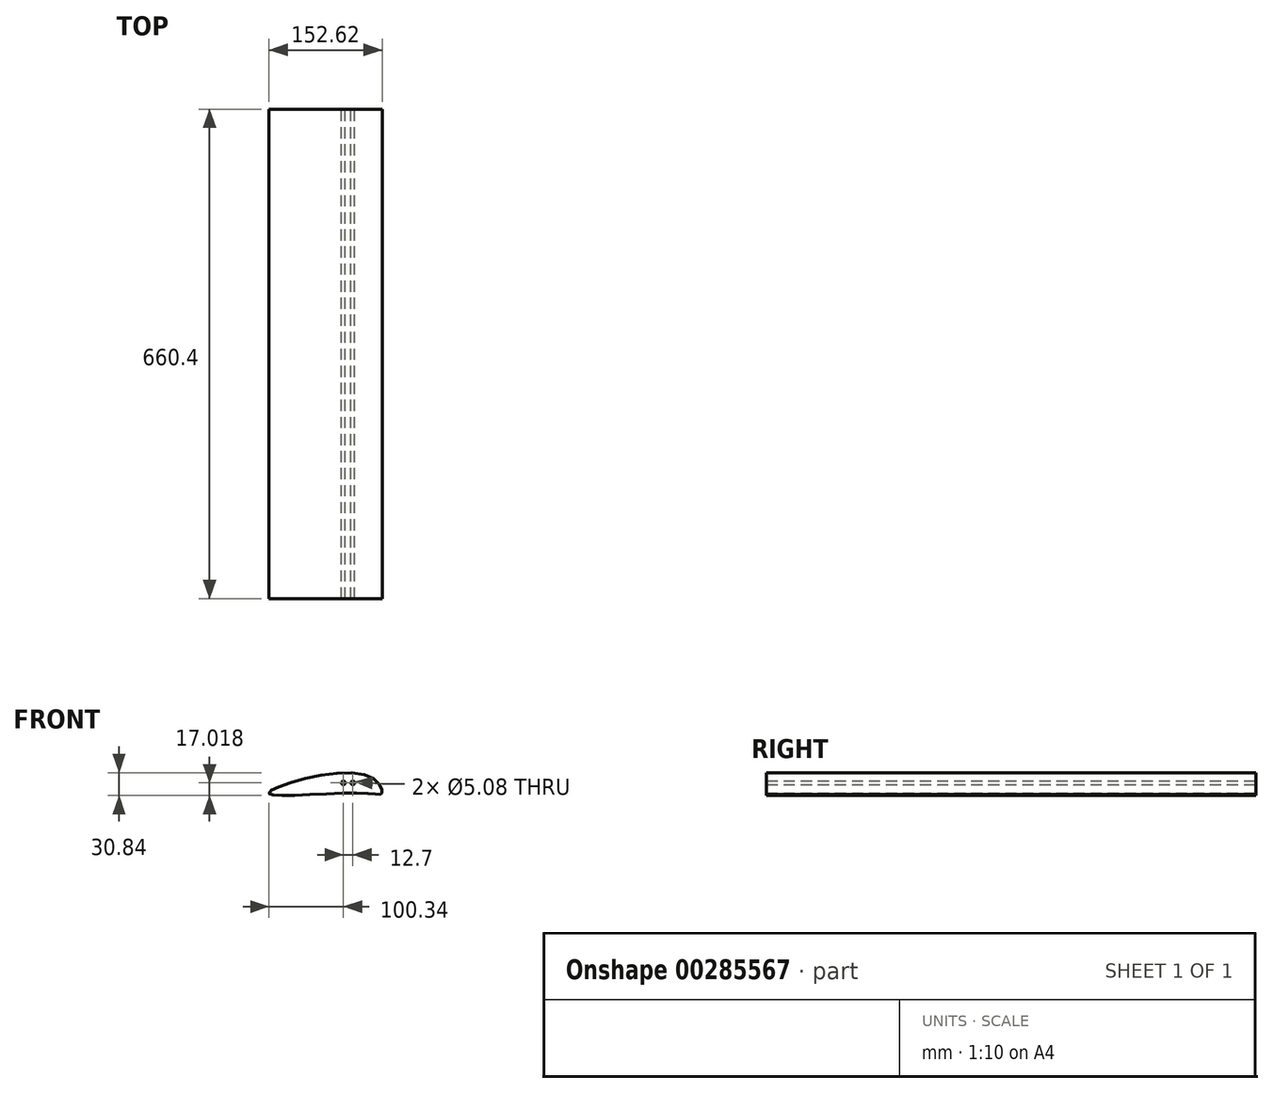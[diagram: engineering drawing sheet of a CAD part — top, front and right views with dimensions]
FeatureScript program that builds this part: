
annotation { "Feature Type Name" : "Feature", "Feature Type Description" : "" }
export const myFeature = defineFeature(function(context is Context, id is Id, definition is map)
    precondition{}
    {
        {
            var Q0;
            Q0=qCreatedBy(makeId("Front.planeOp"),FACE);
            var sketch = newSketch(context, id + "F0", { "sketchPlane" : qUnion([Q0])});
            skFitSpline(sketch, "E0", {"points": [v(39.37, 0) * mm, v(14.25, 25.4) * mm, v(-113.03, 0) * mm, v(15.39, 0) * mm, v(39.37, 0) * mm]});
            skLineSegment(sketch, "E1", {"start": v(0, 0) * mm, "end": v(0, 47.84) * mm, "construction": true});
            skLineSegment(sketch, "E2", {"start": v(-12.7, 43.07) * mm, "end": v(-12.7, -19.6) * mm, "construction": true});
            skLineSegment(sketch, "E3", {"start": v(-20.65, 13.74) * mm, "end": v(12.68, 13.74) * mm, "construction": true});
            skCircle(sketch, "E4", {"center": v(0, 13.74) * mm, "radius": 2.54 * mm});
            skCircle(sketch, "E5", {"center": v(-12.7, 13.74) * mm, "radius": 2.54 * mm});
            skSolve(sketch);
        }
        {
            var Q0;
            Q0 = qSketchRegion(id + "F0", true);
            extrude(context, id + "F1", {"entities" : qUnion([Q0]), "depth" : 660.4 * mm});
        }
    });
